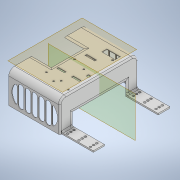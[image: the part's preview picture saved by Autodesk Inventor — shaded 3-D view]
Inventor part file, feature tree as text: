
AUTODESK INVENTOR PART (.ipt)
format: ipt  version: 2020 (Build 240168000, 168)  size: 584,704 bytes
history: native  units: in
note: dims shown in document units (in); Inventor stores cm internally (conversion verified against a paired STEP export)
features: extrude x11, projected_geometry x11, sketch x10, mirror x3, fillet x3, plane x2, shell x1, pattern_linear x1
ambient origin geometry x8: Origin, YZ Plane, XZ Plane, XY Plane, X Axis, Y Axis, Z Axis, Center Point
bodies: Solid1 (feature_tree)
feature tree (42):
  extrude  "Extrusion1"  Depth=6.8701in
  shell  "Shell1"  Thickness=6.8701in
  extrude  "Extrusion3"  Depth=2.7559in TaperAngle=0.0deg
  extrude  "Extrusion4"  Depth=0.125in TaperAngle=0.0deg
  plane  "Work Plane1"
  mirror  "Mirror1"
  extrude  "Extrusion5"  Depth=1.0in
  extrude  "Extrusion6"  Depth=0.1875in
  mirror  "Mirror2"
  extrude  "Extrusion8"  Depth=0.1875in
  extrude  "Extrusion9"  Depth=0.125in
  pattern_linear  "Rectangular Pattern2"  Spacing1=0.1875in  [1 undecoded]
  mirror  "Mirror3"
  extrude  "Extrusion10"  Depth=0.5in
  fillet  "Fillet1"  Radius=0.1875in
  fillet  "Fillet2"  Radius=0.815in
  extrude  "Extrusion11"  Depth=0.5in
  extrude  "Extrusion12"  Depth=0.5in
  fillet  "Fillet5"  Radius=0.5236in
  extrude  "Extrusion13"  Depth=0.3937in TaperAngle=0.0deg
  plane  "Work Plane2"
  sketch  "Sketch3"  dims[d0=4.7244in d1=3.189in d2=6.8701in]
  sketch  "Sketch5"  dims[d4=5.3543in d5=2.7559in d6=0.0in]
  projected_geometry  "Projected Loop3"
  projected_geometry  "Projected Loop4"
  sketch  "Sketch6"  dims[d7=0.0492in d12=0.125in d13=0.0in]
  projected_geometry  "Projected Loop5"
  sketch  "Sketch7"  dims[d18=0.815in d19=1.0in]
  projected_geometry  "Projected Loop6"
  projected_geometry  "Projected Loop7"
  sketch  "Sketch9"  dims[d20=1.0in d21=0.1875in]
  projected_geometry  "Projected Loop9"
  sketch  "Sketch10"  dims[d22=0.1875in d23=0.1875in]
  projected_geometry  "Projected Loop10"
  sketch  "Sketch11"  dims[d24=0.125in d25=0.0in d27=2.5591in]
  projected_geometry  "Projected Loop11"
  sketch  "Sketch12"  dims[d28=0.125in d29=0.0in]
  projected_geometry  "Projected Loop12"
  sketch  "Sketch13"  dims[d30=0.8661in d31=0.0in]
  projected_geometry  "Projected Loop13"
  sketch  "Sketch14"  dims[d40=1.0236in d41=0.1875in d42=0.1875in d43=0.1875in d44=0.815in d45=1.0in d46=1.0in d47=0.5236in d48=0.3937in d49=0.0in d50=0.1575in d51=0.3937in d52=0.0in d53=0.7874in d55=0.2756in d56=0.7874in d58=0.2756in d59=0.125in d60=4.1732in d61=2.2904in d62=1.7717in d63=2.1654in d64=1.1811in d66=1.159in d67=0.8661in d68=0.0in d69=0.1in d70=1.8898in d71=0.1in d72=0.5in d80=0.25in d81=1.9685in d83=0.6in d84=0.3937in d86=1.0in d88=1.0in d89=0.0in d90=1.5748in d91=1.0in d92=0.0in d107=0.68in d108=0.5in d109=0.1378in d110=0.1378in d111=0.1575in d112=0.1575in d114=0.68in d115=0.5in d117=0.5in d118=0.5in d119=0.125in d120=0.1378in d121=0.1378in d122=0.1575in d123=0.1575in d124=0.125in d125=0.125in d126=0.5in d127=0.35in d128=0.857in d129=0.5in d130=0.1378in d131=0.1378in d132=0.1575in d133=0.1575in d134=0.375in d135=0.2559in d136=0.35in d137=1.5in d146=0.1988in d147=0.3209in d148=0.1575in d149=0.1378in d150=1.0in d151=0.5in d152=0.68in d153=0.1575in d154=1.1811in d155=0.68in d156=0.1575in d157=1.1811in d158=0.857in d159=0.1575in d160=1.1811in d161=1.0in d162=0.0in d163=0.4724in d164=0.4528in d165=1.1811in d166=0.15in d167=0.1575in d168=0.0831in d10=0.5in d11=0.0344in]
  projected_geometry  "Projected Loop14"
note: 1 required parameter value undecoded (feature->parameter linkage not recoverable at this tier; creation-order binding heuristic only, values carry confidence <= 0.55)
